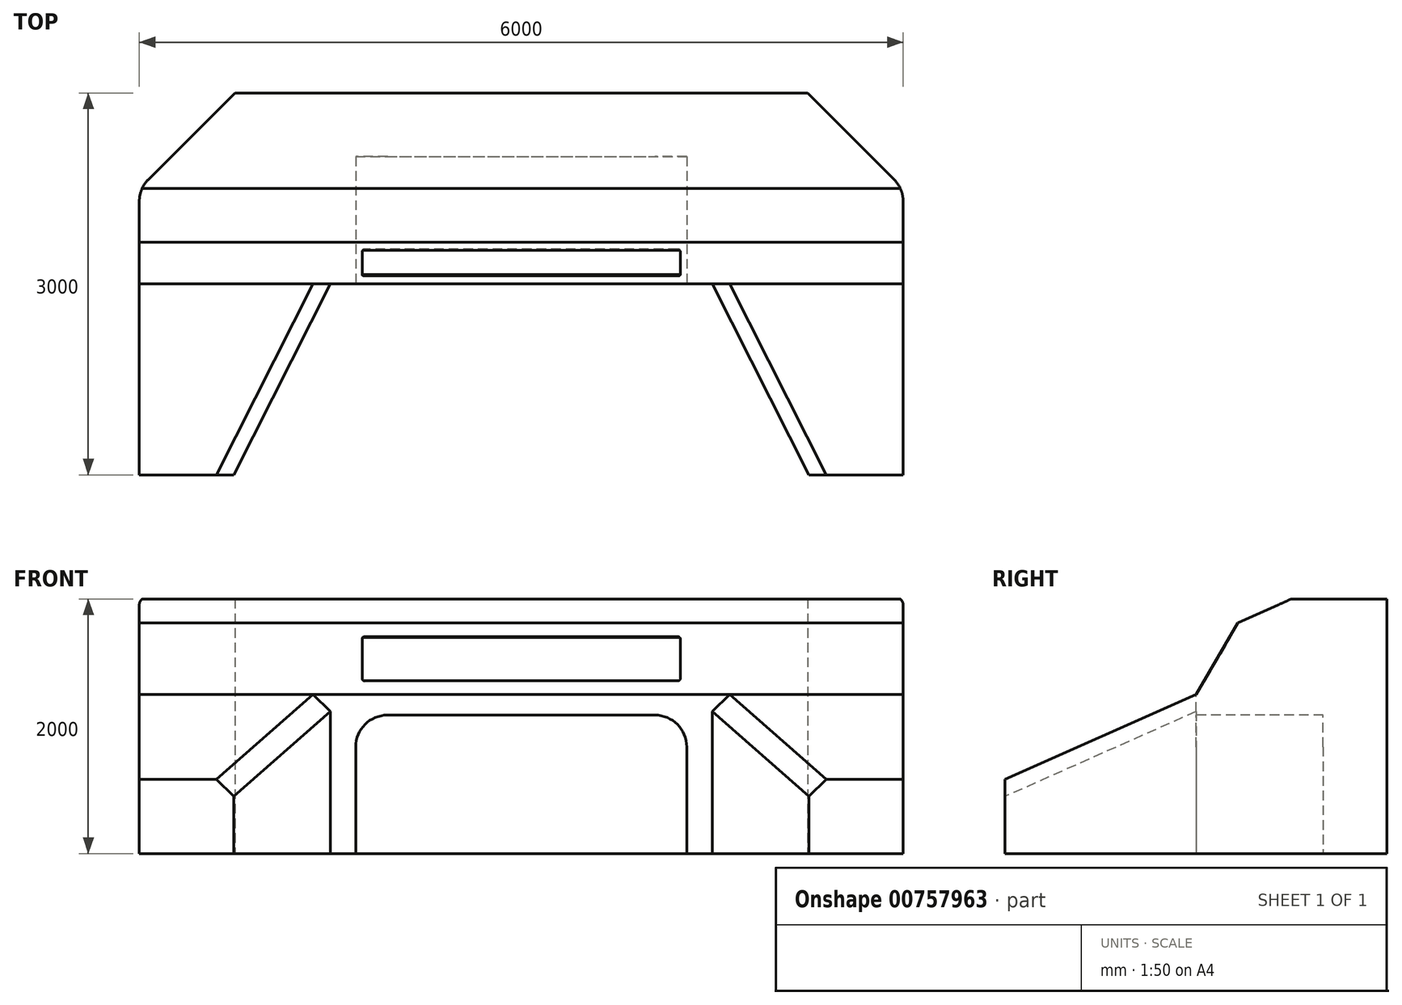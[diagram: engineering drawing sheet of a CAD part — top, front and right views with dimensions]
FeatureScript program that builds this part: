
annotation { "Feature Type Name" : "Feature", "Feature Type Description" : "" }
export const myFeature = defineFeature(function(context is Context, id is Id, definition is map)
    precondition{}
    {
        {
            var Q0;
            Q0=qCreatedBy(makeId("Top.planeOp"),FACE);
            var sketch = newSketch(context, id + "F0", { "sketchPlane" : qUnion([Q0])});
            skLineSegment(sketch, "E0.bottom", {"start": v(3000, -1500) * mm, "end": v(-3000, -1500) * mm, "construction": true});
            skLineSegment(sketch, "E0.top", {"start": v(3000, 1500) * mm, "end": v(-3000, 1500) * mm, "construction": true});
            skLineSegment(sketch, "E0.left", {"start": v(3000, -1500) * mm, "end": v(3000, 0) * mm, "construction": true});
            skLineSegment(sketch, "E0.right", {"start": v(-3000, -1500) * mm, "end": v(-3000, 0) * mm, "construction": true});
            skPoint(sketch, "E0.middle", {"position": v(0, 0) * mm});
            skLineSegment(sketch, "E1", {"start": v(0, 1500) * mm, "end": v(0, -1500) * mm, "construction": true});
            skLineSegment(sketch, "E2", {"start": v(-3000, 0) * mm, "end": v(3000, 0) * mm, "construction": true});
            skLineSegment(sketch, "E3", {"start": v(-2258.4, -1500) * mm, "end": v(-1500, 0) * mm});
            skLineSegment(sketch, "E4.MirrorCS", {"start": v(2258.4, -1500) * mm, "end": v(1500, 0) * mm});
            skLineSegment(sketch, "E5", {"start": v(-1500, 0) * mm, "end": v(1500, 0) * mm});
            skLineSegment(sketch, "E6", {"start": v(-2258.4, -1500) * mm, "end": v(-3000, -1500) * mm});
            skLineSegment(sketch, "E7", {"start": v(-3000, 0) * mm, "end": v(-3000, 1500) * mm, "construction": true});
            skLineSegment(sketch, "E8", {"start": v(3000, 0) * mm, "end": v(3000, 1500) * mm, "construction": true});
            skLineSegment(sketch, "E9", {"start": v(-3000, 750) * mm, "end": v(-2250, 1500) * mm});
            skLineSegment(sketch, "E10.MirrorCS", {"start": v(3000, 750) * mm, "end": v(2250, 1500) * mm});
            skLineSegment(sketch, "E11", {"start": v(-3000, 750) * mm, "end": v(-3000, -1500) * mm});
            skLineSegment(sketch, "E12", {"start": v(-3000, -1500) * mm, "end": v(-2258.4, -1500) * mm});
            skLineSegment(sketch, "E13", {"start": v(2258.4, -1500) * mm, "end": v(3000, -1500) * mm});
            skLineSegment(sketch, "E14", {"start": v(3000, -1500) * mm, "end": v(3000, 750) * mm});
            skLineSegment(sketch, "E15", {"start": v(2250, 1500) * mm, "end": v(-2250, 1500) * mm});
            skSolve(sketch);
        }
        {
            var Q0;
            Q0=makeQuery(id+"F0.imprint","IMPRINT",FACE,{"disambiguationData":[TD([[makeQuery(id+"F0.imprint","IMPRINT",EDGE,{"derivedFrom":sQuery(id+"F0.wireOp",EDGE,"E3")}),1.0]])]});
            extrude(context, id + "F1", {"entities" : qUnion([Q0]), "depth" : 2000 * mm, "offsetDistance" : 25 * mm});
        }
        {
            var Q0;
            Q0=makeQuery(id+"F1.opExtrude","SWEPT_FACE",FACE,{"disambiguationData":[OSD([sQuery(id+"F0.wireOp",EDGE,"E11")])]});
            var sketch = newSketch(context, id + "F2", { "sketchPlane" : qUnion([Q0])});
            skLineSegment(sketch, "E16", {"start": v(-750, 2000) * mm, "end": v(1500, 1000) * mm});
            skLineSegment(sketch, "E17", {"start": v(-327.83, 1812.37) * mm, "end": v(0, 1248.97) * mm});
            skLineSegment(sketch, "E18", {"start": v(0, 1248.97) * mm, "end": v(1500, 582.3) * mm});
            skPoint(sketch, "E19.0", {"position": v(0, 2000) * mm});
            skSolve(sketch);
        }
        {
            var Q0;
            {var subQ0=sQuery(id+"F2.wireOp",EDGE,"E16");Q0=makeQuery(id+"F2.imprint","IMPRINT",FACE,{"disambiguationData":[TD([[makeQuery(id+"F2.imprint","IMPRINT",EDGE,{"derivedFrom":subQ0}),1.0]])]});}
            var Q1;
            {var subQ3=sQuery(id+"F2.wireOp",EDGE,"E17");Q1=makeQuery(id+"F2.imprint","IMPRINT",FACE,{"disambiguationData":[TD([[makeQuery(id+"F2.imprint","IMPRINT",EDGE,{"derivedFrom":subQ3}),1.0]])]});}
            extrude(context, id + "F3", {"entities" : qUnion([Q0, Q1]), "operationType" : NewBodyOperationType.REMOVE, "endBound" : BoundingType.THROUGH_ALL, "oppositeDirection" : true, "depth" : 25 * mm, "offsetDistance" : 25 * mm});
        }
        {
            var Q0;
            Q0=makeQuery(id+"F3.boolean.opBoolean","INTERSECT",EDGE,{"derivedFrom":[makeQuery(id+"F1.opExtrude","SWEPT_FACE",FACE,{"disambiguationData":[OSD([sQuery(id+"F0.wireOp",EDGE,"E3")])]}),makeQuery(id+"F3.opExtrude","SWEPT_FACE",FACE,{"disambiguationData":[OSD([sQuery(id+"F2.wireOp",EDGE,"E18")])]})]});
            var Q1;
            Q1=makeQuery(id+"F3.boolean.opBoolean","INTERSECT",EDGE,{"derivedFrom":[makeQuery(id+"F1.opExtrude","SWEPT_FACE",FACE,{"disambiguationData":[OSD([sQuery(id+"F0.wireOp",EDGE,"E4.MirrorCS")])]}),makeQuery(id+"F3.opExtrude","SWEPT_FACE",FACE,{"disambiguationData":[OSD([sQuery(id+"F2.wireOp",EDGE,"E18")])]})]});
            chamfer(context, id + "F4", {"entities" : qUnion([Q0, Q1]), "width" : 150 * mm, "tangentPropagation" : true});
        }
        {
            var Q0;
            Q0=makeQuery(id+"F1.opExtrude","SWEPT_FACE",FACE,{"disambiguationData":[OSD([sQuery(id+"F0.wireOp",EDGE,"E5")])]});
            var sketch = newSketch(context, id + "F5", { "sketchPlane" : qUnion([Q0])});
            skLineSegment(sketch, "E20", {"start": v(-1500, 1087.6) * mm, "end": v(1500, 1087.6) * mm});
            skLineSegment(sketch, "E21.bottom", {"start": v(-1300, 1087.6) * mm, "end": v(1300, 1087.6) * mm});
            skLineSegment(sketch, "E21.top", {"start": v(-1300, 0) * mm, "end": v(1300, 0) * mm});
            skLineSegment(sketch, "E21.left", {"start": v(-1300, 1087.6) * mm, "end": v(-1300, 0) * mm});
            skLineSegment(sketch, "E21.right", {"start": v(1300, 1087.6) * mm, "end": v(1300, 0) * mm});
            skSolve(sketch);
        }
        {
            var Q0;
            Q0=makeQuery(id+"F5.imprint","IMPRINT",FACE,{"disambiguationData":[TD([[makeQuery(id+"F5.imprint","IMPRINT",EDGE,{"derivedFrom":sQuery(id+"F5.wireOp",EDGE,"E21.top")}),1.0]])]});
            extrude(context, id + "F6", {"entities" : qUnion([Q0]), "operationType" : NewBodyOperationType.REMOVE, "oppositeDirection" : true, "depth" : 1000 * mm, "offsetDistance" : 25 * mm});
        }
        {
            var Q0;
            Q0=makeQuery(id+"F3.boolean.opBoolean","COPY",FACE,{"derivedFrom":makeQuery(id+"F3.opExtrude","SWEPT_FACE",FACE,{"disambiguationData":[OSD([sQuery(id+"F2.wireOp",EDGE,"E17")])]})});
            var sketch = newSketch(context, id + "F7", { "sketchPlane" : qUnion([Q0])});
            skLineSegment(sketch, "E22", {"start": v(0, 1731.35) * mm, "end": v(0, 1079.52) * mm, "construction": true});
            skLineSegment(sketch, "E23.bottom", {"start": v(1250, 1205.43) * mm, "end": v(-1250, 1205.43) * mm});
            skLineSegment(sketch, "E23.top", {"start": v(1250, 1605.43) * mm, "end": v(-1250, 1605.43) * mm});
            skLineSegment(sketch, "E23.left", {"start": v(1250, 1205.43) * mm, "end": v(1250, 1605.43) * mm});
            skLineSegment(sketch, "E23.right", {"start": v(-1250, 1205.43) * mm, "end": v(-1250, 1605.43) * mm});
            skPoint(sketch, "E23.middle", {"position": v(0, 1405.43) * mm});
            skSolve(sketch);
        }
        {
            var Q0;
            Q0=makeQuery(id+"F7.imprint","IMPRINT",FACE,{"disambiguationData":[TD([[makeQuery(id+"F7.imprint","IMPRINT",EDGE,{"derivedFrom":sQuery(id+"F7.wireOp",EDGE,"E23.bottom")}),-1.0]])]});
            extrude(context, id + "F8", {"entities" : qUnion([Q0]), "operationType" : NewBodyOperationType.REMOVE, "oppositeDirection" : true, "depth" : 10 * mm, "offsetDistance" : 25 * mm});
        }
        {
            var Q0;
            Q0=makeQuery(id+"F8.boolean.opBoolean","COPY",EDGE,{"derivedFrom":makeQuery(id+"F8.opExtrude","SWEPT_EDGE",EDGE,{"disambiguationData":[OSD([sQuery(id+"F7.wireOp",EDGE,"E23.bottom"),sQuery(id+"F7.wireOp",EDGE,"E23.right")])]})});
            var Q1;
            Q1=makeQuery(id+"F8.boolean.opBoolean","COPY",EDGE,{"derivedFrom":makeQuery(id+"F8.opExtrude","SWEPT_EDGE",EDGE,{"disambiguationData":[OSD([sQuery(id+"F7.wireOp",EDGE,"E23.top"),sQuery(id+"F7.wireOp",EDGE,"E23.right")])]})});
            var Q2;
            Q2=makeQuery(id+"F8.boolean.opBoolean","COPY",EDGE,{"derivedFrom":makeQuery(id+"F8.opExtrude","SWEPT_EDGE",EDGE,{"disambiguationData":[OSD([sQuery(id+"F7.wireOp",EDGE,"E23.top"),sQuery(id+"F7.wireOp",EDGE,"E23.left")])]})});
            var Q3;
            Q3=makeQuery(id+"F8.boolean.opBoolean","COPY",EDGE,{"derivedFrom":makeQuery(id+"F8.opExtrude","SWEPT_EDGE",EDGE,{"disambiguationData":[OSD([sQuery(id+"F7.wireOp",EDGE,"E23.bottom"),sQuery(id+"F7.wireOp",EDGE,"E23.left")])]})});
            fillet(context, id + "F9", {"entities" : qUnion([Q0, Q1, Q2, Q3]), "radius" : 19.3 * mm, "tangentPropagation" : true, "allowEdgeOverflow" : false});
        }
        {
            var Q0;
            Q0=makeQuery(id+"F1.opExtrude","SWEPT_EDGE",EDGE,{"disambiguationData":[OSD([sQuery(id+"F0.wireOp",EDGE,"E9"),sQuery(id+"F0.wireOp",EDGE,"E11")])]});
            var Q1;
            Q1=makeQuery(id+"F3.boolean.opBoolean","COPY",EDGE,{"derivedFrom":makeQuery(id+"F3.opExtrude","SWEPT_EDGE",EDGE,{"disambiguationData":[OSD([sQuery(id+"F0.wireOp",EDGE,"E9"),sQuery(id+"F0.wireOp",EDGE,"E11"),sQuery(id+"F2.wireOp",EDGE,"E16")])]})});
            var Q2;
            Q2=makeQuery(id+"F1.opExtrude","SWEPT_EDGE",EDGE,{"disambiguationData":[OSD([sQuery(id+"F0.wireOp",EDGE,"E10.MirrorCS"),sQuery(id+"F0.wireOp",EDGE,"E14")])]});
            fillet(context, id + "F10", {"entities" : qUnion([Q0, Q1, Q2]), "radius" : 242.74 * mm, "tangentPropagation" : true, "allowEdgeOverflow" : false});
        }
        {
            var Q0;
            Q0=makeQuery(id+"F6.boolean.opBoolean","COPY",EDGE,{"derivedFrom":makeQuery(id+"F6.opExtrude","SWEPT_EDGE",EDGE,{"disambiguationData":[OSD([sQuery(id+"F5.wireOp",EDGE,"E20"),sQuery(id+"F5.wireOp",EDGE,"E21.left")])]})});
            var Q1;
            Q1=makeQuery(id+"F6.boolean.opBoolean","COPY",EDGE,{"derivedFrom":makeQuery(id+"F6.opExtrude","SWEPT_EDGE",EDGE,{"disambiguationData":[OSD([sQuery(id+"F5.wireOp",EDGE,"E20"),sQuery(id+"F5.wireOp",EDGE,"E21.right")])]})});
            fillet(context, id + "F11", {"entities" : qUnion([Q0, Q1]), "radius" : 250 * mm, "tangentPropagation" : true, "allowEdgeOverflow" : false});
        }
    });
